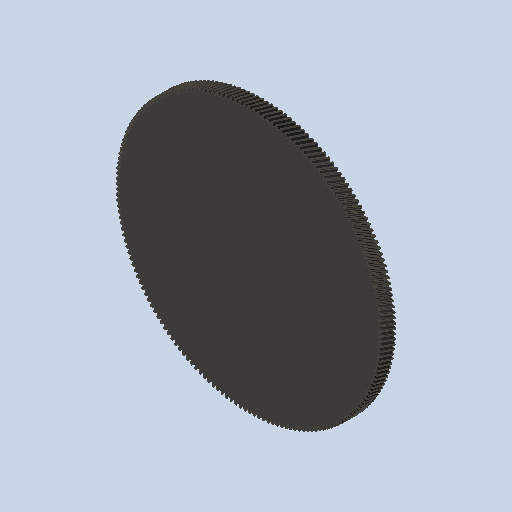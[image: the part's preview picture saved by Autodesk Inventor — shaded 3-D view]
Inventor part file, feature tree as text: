
AUTODESK INVENTOR PART (.ipt)
format: ipt  version: 2023 (Build 270158000, 158)  size: 2,009,088 bytes
history: native  units: mm (DEFAULTED — no unit token found)
features: plane x3, other x3, sketch x2, extrude x1
ambient origin geometry x8: Origin, YZ Plane, XZ Plane, XY Plane, X Axis, Y Axis, Z Axis, Center Point
bodies: Solid1 (feature_tree)
feature tree (9):
  extrude  "Extrusion1"  Depth=10.0mm TaperAngle=0.0deg
  plane  "Work Plane2"
  plane  "Work Plane8"
  plane  "Work Plane9"
  other  "Spur Gear"
  sketch  "Sketch1"  dims[d0=193.423911mm d1=10.0mm d2=0.0mm]
  sketch  "Sketch2"  dims[d3=191.551999mm d4=10.0mm d5=0.0mm d16=107.95mm d17=0.0mm d34=0.174533mm d39=0.0mm d41=0.0mm d43=107.95mm d46=107.95mm d47=0.0mm d48=0.0mm]
  other  "Srf1"
  other  "Pitch Diameter"
